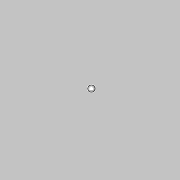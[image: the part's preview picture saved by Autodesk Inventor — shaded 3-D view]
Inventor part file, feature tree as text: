
AUTODESK INVENTOR PART (.ipt)
format: ipt  version: 2017 (Build 210142000, 142)  size: 135,168 bytes
history: native  units: mm
features: sketch x6, extrude x5, revolve x1, thread x1
ambient origin geometry x8: Origin, YZ Plane, XZ Plane, XY Plane, X Axis, Y Axis, Z Axis, Center Point
bodies: Solid1 (feature_tree)
feature tree (13):
  revolve  "Revolution1"  [1 undecoded]
  extrude  "Extrusion1"  Depth=24.0mm
  extrude  "Extrusion2"  Depth=36.0mm
  extrude  "Extrusion3"  Depth=44.0mm
  extrude  "Extrusion4"  TaperAngle=90.0deg  [1 undecoded]
  thread  "Thread1"  [1 undecoded]
  extrude  "Extrusion6"  Depth=20.0mm TaperAngle=0.0deg
  sketch  "Sketch1"  dims[d0=79.0mm d2=18.0mm]
  sketch  "Sketch2"  dims[d3=33.2mm d4=24.0mm]
  sketch  "Sketch3"  dims[d5=21.0mm d6=36.0mm]
  sketch  "Sketch4"  dims[d7=151.0mm d9=44.0mm]
  sketch  "Sketch5"  dims[d10=34.0mm d11=90.0deg d12=10.0mm d13=0.0mm]
  sketch  "Sketch7"  dims[d14=20.0mm d15=20.0mm d16=0.0mm d17=2.0mm d18=2.0mm d19=0.0mm d20=4.0mm d21=0.0mm d22=10.0mm d23=0.0mm d27=36.0mm d28=15.0mm d29=0.0mm d30=0.0mm]
note: 3 required parameter values undecoded (feature->parameter linkage not recoverable at this tier; creation-order binding heuristic only, values carry confidence <= 0.55)